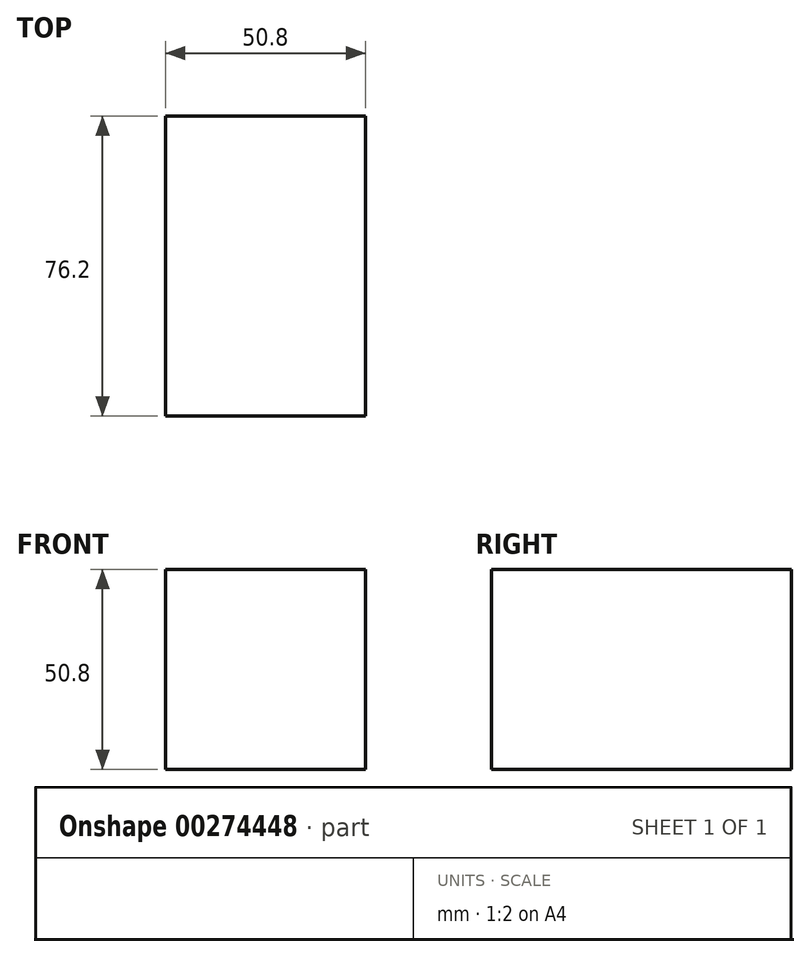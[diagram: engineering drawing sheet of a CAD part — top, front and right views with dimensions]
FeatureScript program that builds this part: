
annotation { "Feature Type Name" : "Feature", "Feature Type Description" : "" }
export const myFeature = defineFeature(function(context is Context, id is Id, definition is map)
    precondition{}
    {
        {
            var Q0;
            Q0=qCreatedBy(makeId("Front.planeOp"),FACE);
            var sketch = newSketch(context, id + "F0", { "sketchPlane" : qUnion([Q0])});
            skLineSegment(sketch, "E0", {"start": v(-69.7, 62.25) * mm, "end": v(-18.9, 62.25) * mm});
            skLineSegment(sketch, "E1", {"start": v(-18.9, 62.25) * mm, "end": v(-18.9, 11.45) * mm});
            skLineSegment(sketch, "E2", {"start": v(-18.9, 11.45) * mm, "end": v(-69.7, 11.45) * mm});
            skLineSegment(sketch, "E3", {"start": v(-69.7, 11.45) * mm, "end": v(-69.7, 62.25) * mm});
            skSolve(sketch);
        }
        {
            var Q0;
            Q0=makeQuery(id+"F0.imprint","IMPRINT",FACE,{"disambiguationData":[TD([[makeQuery(id+"F0.imprint","IMPRINT",EDGE,{"derivedFrom":sQuery(id+"F0.wireOp",EDGE,"E0")}),-1.0]])]});
            extrude(context, id + "F1", {"entities" : qUnion([Q0]), "depth" : 76.2 * mm});
        }
    });
